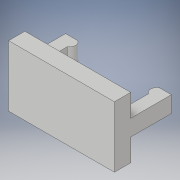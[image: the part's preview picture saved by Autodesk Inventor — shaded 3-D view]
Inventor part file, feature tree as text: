
AUTODESK INVENTOR PART (.ipt)
format: ipt  version: 2019 (Build 230136000, 136)  size: 134,656 bytes
history: native  units: in
note: dims shown in document units (in); Inventor stores cm internally (conversion verified against a paired STEP export)
features: extrude x4, sketch x3, projected_geometry x1
ambient origin geometry x8: Origin, YZ Plane, XZ Plane, XY Plane, X Axis, Y Axis, Z Axis, Center Point
bodies: Solid1 (feature_tree)
feature tree (8):
  sketch  "Sketch2"  dims[d0=1.0236in d1=0.1575in d2=0.0in]
  extrude  "Extrusion1"  Depth=0.1575in TaperAngle=0.0deg
  extrude  "Extrusion2"  Depth=0.0787in
  extrude  "Extrusion3"  Depth=0.1575in
  extrude  "Extrusion4"  Depth=0.0787in TaperAngle=0.0deg
  sketch  "Sketch3"  dims[d3=0.5906in d4=0.0787in]
  projected_geometry  "Projected Loop1"
  sketch  "Sketch4"  dims[d5=0.0787in d6=0.0in d7=0.1575in d9=0.0787in d10=0.4724in d11=0.0in d12=0.0in d13=0.0591in d14=0.0295in d15=0.1575in d16=0.0in d17=0.1181in d18=0.0787in d19=0.1181in d20=0.1181in]
